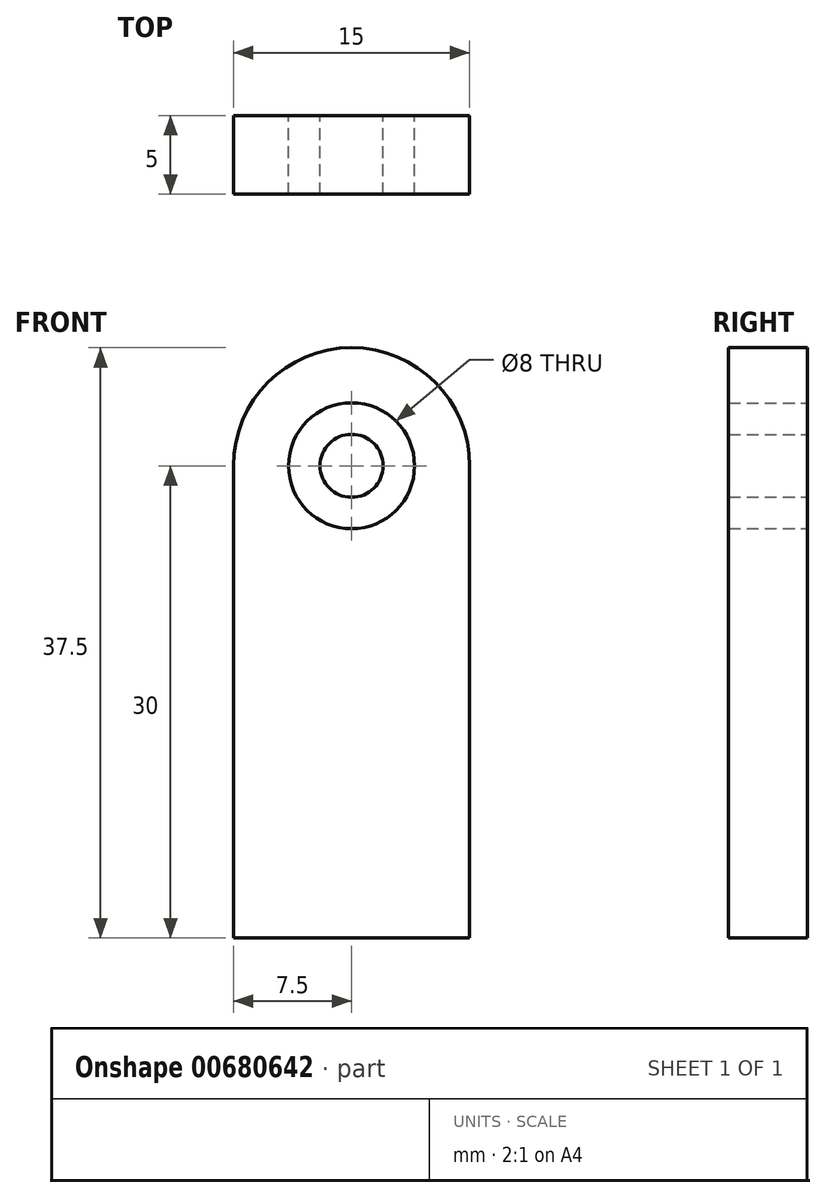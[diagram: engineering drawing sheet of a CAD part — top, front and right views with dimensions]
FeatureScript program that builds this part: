
annotation { "Feature Type Name" : "Feature", "Feature Type Description" : "" }
export const myFeature = defineFeature(function(context is Context, id is Id, definition is map)
    precondition{}
    {
        {
            var Q0;
            Q0=qCreatedBy(makeId("Front.planeOp"),FACE);
            var sketch = newSketch(context, id + "F0", { "sketchPlane" : qUnion([Q0])});
            skLineSegment(sketch, "E0.bottom", {"start": v(0, 0) * mm, "end": v(15, 0) * mm});
            skLineSegment(sketch, "E0.left", {"start": v(0, 0) * mm, "end": v(0, 30) * mm});
            skLineSegment(sketch, "E0.right", {"start": v(15, 0) * mm, "end": v(15, 30) * mm});
            skArc(sketch, "E1", {"start": v(15, 30) * mm, "mid": v(7.5, 37.5) * mm, "end": v(0, 30) * mm});
            skCircle(sketch, "E2", {"center": v(7.5, 30) * mm, "radius": 4 * mm});
            skCircle(sketch, "E3", {"center": v(7.5, 30) * mm, "radius": 2 * mm});
            skSolve(sketch);
        }
        {
            var Q0;
            Q0=makeQuery(id+"F0.imprint","IMPRINT",FACE,{"disambiguationData":[TD([[makeQuery(id+"F0.imprint","IMPRINT",EDGE,{"derivedFrom":sQuery(id+"F0.wireOp",EDGE,"E0.bottom")}),1.0]])]});
            var Q1;
            Q1=makeQuery(id+"F0.imprint","IMPRINT",FACE,{"disambiguationData":[TD([[makeQuery(id+"F0.imprint","IMPRINT",EDGE,{"derivedFrom":sQuery(id+"F0.wireOp",EDGE,"E3")}),1.0]])]});
            extrude(context, id + "F1", {"entities" : qUnion([Q0, Q1]), "depth" : 5 * mm, "offsetDistance" : 25.4 * mm});
        }
    });
